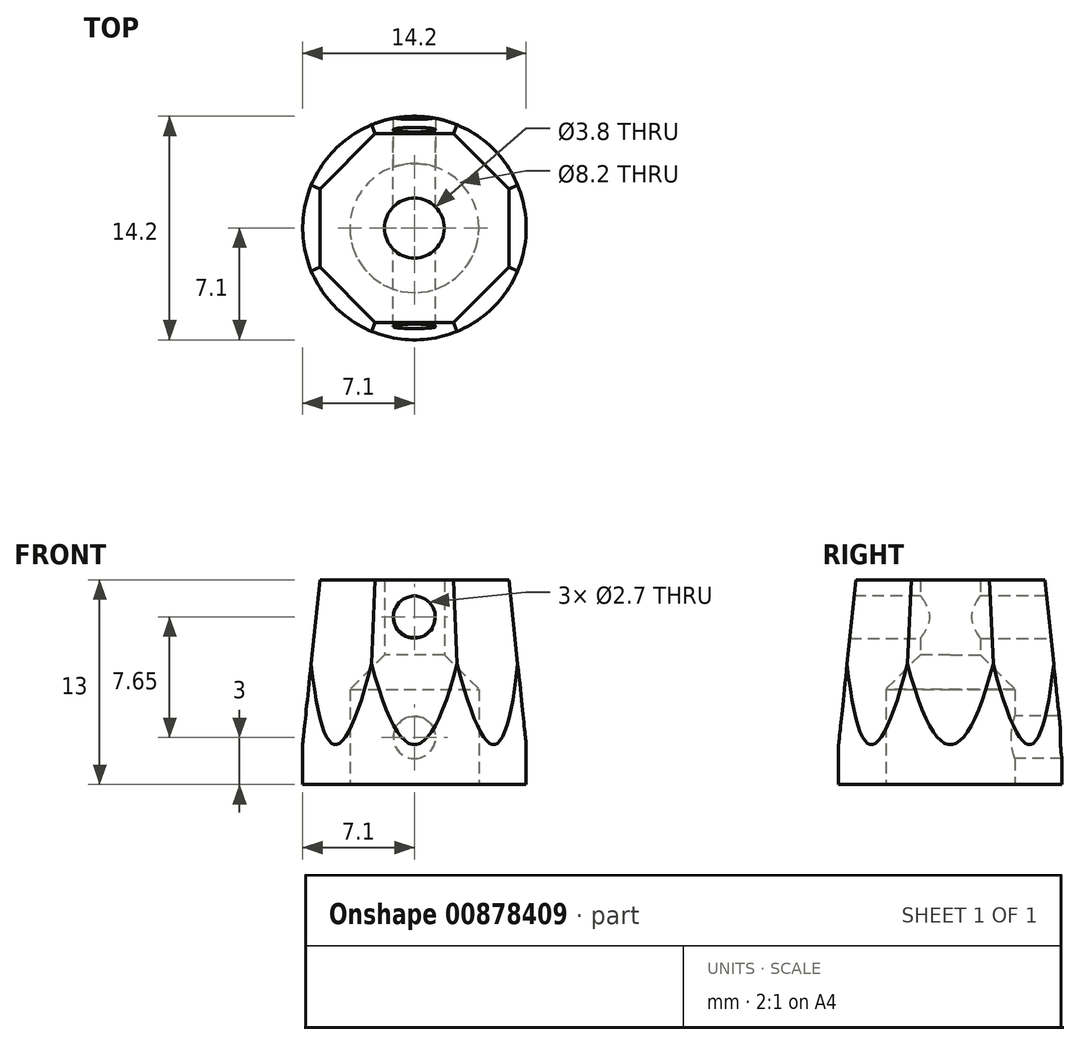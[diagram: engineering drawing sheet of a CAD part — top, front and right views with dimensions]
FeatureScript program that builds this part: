
annotation { "Feature Type Name" : "Feature", "Feature Type Description" : "" }
export const myFeature = defineFeature(function(context is Context, id is Id, definition is map)
    precondition{}
    {
        {
            var Q0;
            Q0=qCreatedBy(makeId("Top.planeOp"),FACE);
            var sketch = newSketch(context, id + "F0", { "sketchPlane" : qUnion([Q0])});
            skCircle(sketch, "E0", {"center": v(0, 0) * mm, "radius": 7.1 * mm});
            skCircle(sketch, "E1", {"center": v(0, 0) * mm, "radius": 4.1 * mm});
            skSolve(sketch);
        }
        {
            var Q0;
            Q0 = qSketchRegion(id + "F0", true);
            extrude(context, id + "F1", {"entities" : qUnion([Q0]), "depth" : 6 * mm, "offsetDistance" : 25 * mm});
        }
        {
            var Q0;
            Q0=qCreatedBy(makeId("Front.planeOp"),FACE);
            var sketch = newSketch(context, id + "F2", { "sketchPlane" : qUnion([Q0])});
            skCircle(sketch, "E2", {"center": v(0, 3) * mm, "radius": 1.35 * mm});
            skLineSegment(sketch, "E3", {"start": v(0, 0) * mm, "end": v(0, 6) * mm, "construction": true});
            skSolve(sketch);
        }
        {
            var Q0;
            Q0 = qSketchRegion(id + "F2", true);
            extrude(context, id + "F3", {"entities" : qUnion([Q0]), "operationType" : NewBodyOperationType.REMOVE, "oppositeDirection" : true, "depth" : 25 * mm, "offsetDistance" : 25 * mm});
        }
        {
            var Q0;
            Q0=qCreatedBy(makeId("Front.planeOp"),FACE);
            var sketch = newSketch(context, id + "F4", { "sketchPlane" : qUnion([Q0])});
            skLineSegment(sketch, "E4", {"start": v(0, 0) * mm, "end": v(0, 9.94) * mm, "construction": true});
            skSolve(sketch);
        }
        {
            var Q0;
            Q0=makeQuery(id+"F1.opExtrude","CAP_FACE",FACE,{"disambiguationData":[OSD([sQuery(id+"F0.wireOp",EDGE,"E0"),sQuery(id+"F0.wireOp",EDGE,"E1")])],"isStart":false});
            var sketch = newSketch(context, id + "F5", { "sketchPlane" : qUnion([Q0])});
            skCircle(sketch, "E5", {"center": v(0, 0) * mm, "radius": 1.9 * mm});
            skCircle(sketch, "E6.0", {"center": v(0, 0) * mm, "radius": 7.1 * mm});
            skSolve(sketch);
        }
        {
            var Q0;
            Q0 = qSketchRegion(id + "F5", true);
            extrude(context, id + "F6", {"entities" : qUnion([Q0]), "operationType" : NewBodyOperationType.ADD, "depth" : 7 * mm, "offsetDistance" : 25 * mm});
        }
        {
            var Q0;
            Q0=qCreatedBy(makeId("Front.planeOp"),FACE);
            var sketch = newSketch(context, id + "F7", { "sketchPlane" : qUnion([Q0])});
            skCircle(sketch, "E7", {"center": v(0, 10.65) * mm, "radius": 1.35 * mm});
            skLineSegment(sketch, "E8", {"start": v(0, 10.65) * mm, "end": v(0, 12) * mm, "construction": true});
            skLineSegment(sketch, "E9", {"start": v(0, 12) * mm, "end": v(0, 13) * mm, "construction": true});
            skSolve(sketch);
        }
        {
            var Q0;
            Q0 = qSketchRegion(id + "F7", true);
            extrude(context, id + "F8", {"entities" : qUnion([Q0]), "operationType" : NewBodyOperationType.REMOVE, "endBound" : BoundingType.THROUGH_ALL, "depth" : 25 * mm, "offsetDistance" : 25 * mm, "hasSecondDirection" : true, "secondDirectionBound" : SecondDirectionBoundingType.THROUGH_ALL, "secondDirectionOppositeDirection" : true, "secondDirectionDepth" : 25 * mm});
        }
        {
            var Q0;
            Q0=makeQuery(id+"F6.opExtrude","CAP_EDGE",EDGE,{"disambiguationData":[OSD([sQuery(id+"F5.wireOp",EDGE,"E5")])],"isStart":true});
            chamfer(context, id + "F9", {"entities" : qUnion([Q0]), "width" : 2.25 * mm, "tangentPropagation" : true});
        }
        {
            var Q0;
            Q0=makeQuery(id+"F6.opExtrude","CAP_FACE",FACE,{"disambiguationData":[OSD([sQuery(id+"F5.wireOp",EDGE,"E5"),sQuery(id+"F5.wireOp",EDGE,"E6.0")])],"isStart":false});
            var sketch = newSketch(context, id + "F10", { "sketchPlane" : qUnion([Q0])});
            skCircle(sketch, "E10.cCircle", {"center": v(0, 0) * mm, "radius": 6 * mm, "construction": true});
            skLineSegment(sketch, "E10.0", {"start": v(2.49, 6) * mm, "end": v(6, 2.49) * mm});
            skLineSegment(sketch, "E10.1", {"start": v(6, 2.49) * mm, "end": v(6, -2.49) * mm});
            skLineSegment(sketch, "E10.2", {"start": v(6, -2.49) * mm, "end": v(2.49, -6) * mm});
            skLineSegment(sketch, "E10.3", {"start": v(2.49, -6) * mm, "end": v(-2.49, -6) * mm});
            skLineSegment(sketch, "E10.4", {"start": v(-2.49, -6) * mm, "end": v(-6, -2.49) * mm});
            skLineSegment(sketch, "E10.5", {"start": v(-6, -2.49) * mm, "end": v(-6, 2.49) * mm});
            skLineSegment(sketch, "E10.6", {"start": v(-6, 2.49) * mm, "end": v(-2.49, 6) * mm});
            skLineSegment(sketch, "E10.7", {"start": v(-2.49, 6) * mm, "end": v(2.49, 6) * mm});
            skPoint(sketch, "E10.0.midPoint", {"position": v(4.24, 4.24) * mm});
            skSolve(sketch);
        }
        {
            var Q0;
            Q0 = qSketchRegion(id + "F10", true);
            extrude(context, id + "F11", {"entities" : qUnion([Q0]), "operationType" : NewBodyOperationType.INTERSECT, "oppositeDirection" : true, "depth" : 25 * mm, "offsetDistance" : 25 * mm, "hasDraft" : true, "draftAngle" : 6 * degree});
        }
    });
